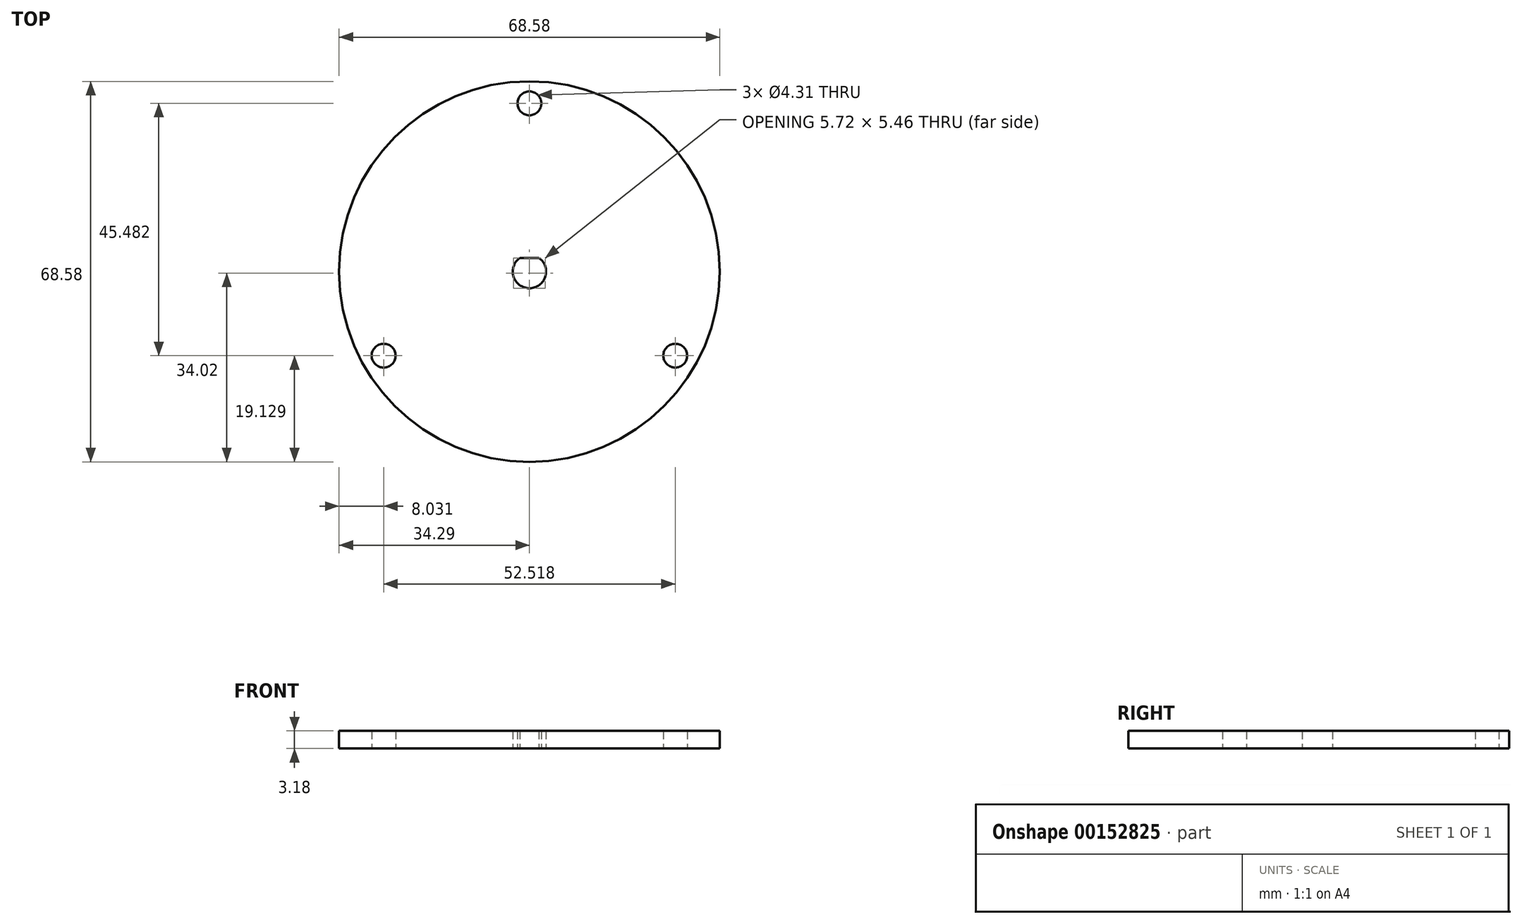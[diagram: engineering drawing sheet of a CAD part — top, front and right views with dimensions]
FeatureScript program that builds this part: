
annotation { "Feature Type Name" : "Feature", "Feature Type Description" : "" }
export const myFeature = defineFeature(function(context is Context, id is Id, definition is map)
    precondition{}
    {
        {
            var Q0;
            Q0=qCreatedBy(makeId("Top.planeOp"),FACE);
            var sketch = newSketch(context, id + "F0", { "sketchPlane" : qUnion([Q0])});
            skArc(sketch, "E0", {"start": v(-1.72, 2.46) * mm, "mid": v(0, -3) * mm, "end": v(1.72, 2.46) * mm});
            skLineSegment(sketch, "E1", {"start": v(-1.72, 2.46) * mm, "end": v(1.72, 2.46) * mm});
            skLineSegment(sketch, "E2", {"start": v(0, 2.46) * mm, "end": v(0, 0) * mm, "construction": true});
            skCircle(sketch, "E3", {"center": v(0, 0) * mm, "radius": 34.3 * mm});
            skCircle(sketch, "E4.cCircle", {"center": v(0, 0) * mm, "radius": 15.16 * mm, "construction": true});
            skLineSegment(sketch, "E4.0", {"start": v(26.26, -15.16) * mm, "end": v(-26.26, -15.16) * mm, "construction": true});
            skLineSegment(sketch, "E4.1", {"start": v(-26.26, -15.16) * mm, "end": v(0, 30.32) * mm, "construction": true});
            skLineSegment(sketch, "E4.2", {"start": v(0, 30.32) * mm, "end": v(26.26, -15.16) * mm, "construction": true});
            skCircle(sketch, "E5", {"center": v(0, 30.32) * mm, "radius": 3.97 * mm, "construction": true});
            skCircle(sketch, "E6", {"center": v(0, 30.32) * mm, "radius": 2.15 * mm});
            skCircle(sketch, "E7", {"center": v(26.26, -15.16) * mm, "radius": 2.15 * mm});
            skCircle(sketch, "E8", {"center": v(-26.26, -15.16) * mm, "radius": 2.15 * mm});
            skSolve(sketch);
        }
        {
            var Q0;
            Q0 = qSketchRegion(id + "F0", true);
            extrude(context, id + "F1", {"entities" : qUnion([Q0]), "depth" : 3.17 * mm});
        }
    });
